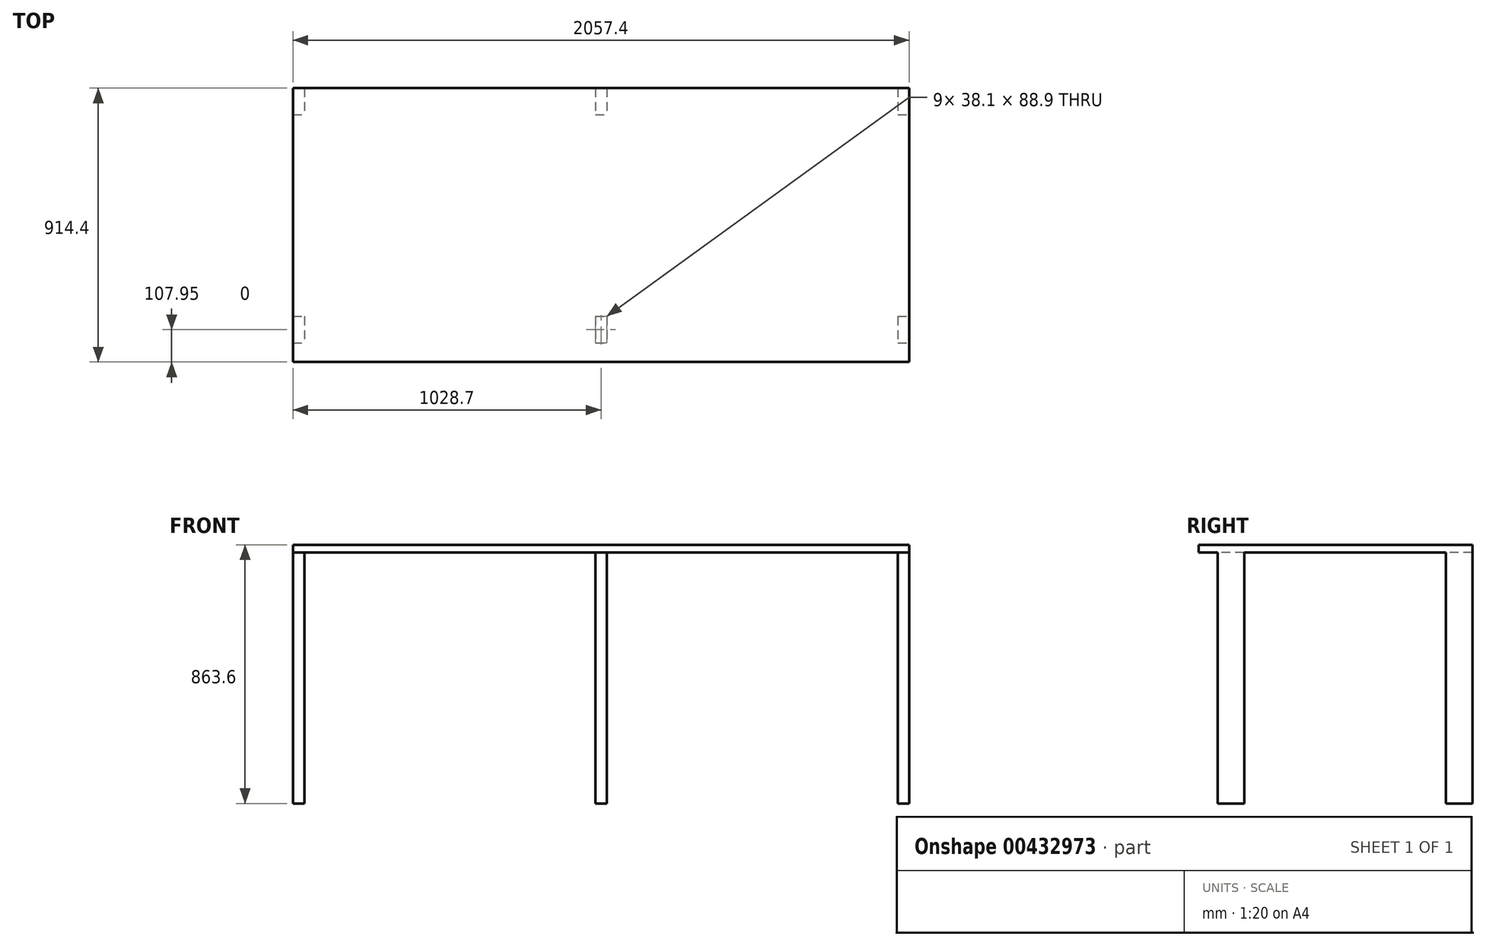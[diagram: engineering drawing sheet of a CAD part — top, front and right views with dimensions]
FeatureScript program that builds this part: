
annotation { "Feature Type Name" : "Feature", "Feature Type Description" : "" }
export const myFeature = defineFeature(function(context is Context, id is Id, definition is map)
    precondition{}
    {
        {
            var Q0;
            Q0=qCreatedBy(makeId("Top.planeOp"),FACE);
            var sketch = newSketch(context, id + "F0", { "sketchPlane" : qUnion([Q0])});
            skLineSegment(sketch, "E0.bottom", {"start": v(1028.7, 457.2) * mm, "end": v(-1028.7, 457.2) * mm});
            skLineSegment(sketch, "E0.top", {"start": v(1028.7, -457.2) * mm, "end": v(-1028.7, -457.2) * mm});
            skLineSegment(sketch, "E0.left", {"start": v(1028.7, 457.2) * mm, "end": v(1028.7, -457.2) * mm});
            skLineSegment(sketch, "E0.right", {"start": v(-1028.7, 457.2) * mm, "end": v(-1028.7, -457.2) * mm});
            skPoint(sketch, "E0.middle", {"position": v(0, 0) * mm});
            skSolve(sketch);
        }
        {
            var Q0;
            Q0=makeQuery(id+"F0.imprint","IMPRINT",FACE,{"disambiguationData":[TD([[makeQuery(id+"F0.imprint","IMPRINT",EDGE,{"derivedFrom":sQuery(id+"F0.wireOp",EDGE,"E0.bottom")}),1.0]])]});
            extrude(context, id + "F1", {"entities" : qUnion([Q0]), "oppositeDirection" : true, "depth" : 863.6 * mm});
        }
        {
            var Q0;
            Q0=makeQuery(id+"F1.opExtrude","SWEPT_FACE",FACE,{"disambiguationData":[OSD([sQuery(id+"F0.wireOp",EDGE,"E0.left")])]});
            var sketch = newSketch(context, id + "F2", { "sketchPlane" : qUnion([Q0])});
            skLineSegment(sketch, "E1", {"start": v(-457.2, 0) * mm, "end": v(-457.2, -25.4) * mm});
            skLineSegment(sketch, "E2", {"start": v(-457.2, -25.4) * mm, "end": v(-393.7, -25.4) * mm});
            skLineSegment(sketch, "E3", {"start": v(-393.7, -25.4) * mm, "end": v(-393.7, -863.6) * mm});
            skLineSegment(sketch, "E4", {"start": v(-393.7, -863.6) * mm, "end": v(-457.2, -863.6) * mm});
            skLineSegment(sketch, "E5", {"start": v(-457.2, -863.6) * mm, "end": v(-457.2, -25.4) * mm});
            skLineSegment(sketch, "E6", {"start": v(-393.7, -25.4) * mm, "end": v(457.2, -25.4) * mm});
            skLineSegment(sketch, "E7", {"start": v(-393.7, -25.4) * mm, "end": v(-304.8, -25.4) * mm});
            skLineSegment(sketch, "E8", {"start": v(-304.8, -25.4) * mm, "end": v(-304.8, -863.6) * mm});
            skLineSegment(sketch, "E9", {"start": v(-304.8, -863.6) * mm, "end": v(368.3, -863.6) * mm});
            skLineSegment(sketch, "E10", {"start": v(368.3, -863.6) * mm, "end": v(368.3, -25.4) * mm});
            skSolve(sketch);
        }
        {
            var Q0;
            Q0=makeQuery(id+"F2.imprint","IMPRINT",FACE,{"disambiguationData":[TD([[makeQuery(id+"F2.imprint","IMPRINT",EDGE,{"derivedFrom":sQuery(id+"F2.wireOp",EDGE,"E2")}),-1.0]])]});
            var Q1;
            {var subQ0=sQuery(id+"F2.wireOp",EDGE,"E8");Q1=makeQuery(id+"F2.imprint","IMPRINT",FACE,{"disambiguationData":[TD([[makeQuery(id+"F2.imprint","IMPRINT",EDGE,{"derivedFrom":subQ0}),1.0]])]});}
            extrude(context, id + "F3", {"entities" : qUnion([Q0, Q1]), "operationType" : NewBodyOperationType.REMOVE, "endBound" : BoundingType.THROUGH_ALL, "oppositeDirection" : true, "depth" : 25.4 * mm});
        }
        {
            var Q0;
            Q0=makeQuery(id+"F3.boolean.opBoolean","COPY",FACE,{"derivedFrom":makeQuery(id+"F3.opExtrude","SWEPT_FACE",FACE,{"disambiguationData":[OSD([sQuery(id+"F2.wireOp",EDGE,"E3")])]})});
            var sketch = newSketch(context, id + "F4", { "sketchPlane" : qUnion([Q0])});
            skLineSegment(sketch, "E11", {"start": v(-1028.7, -863.6) * mm, "end": v(-990.6, -863.6) * mm});
            skLineSegment(sketch, "E12", {"start": v(-990.6, -863.6) * mm, "end": v(-990.6, -25.4) * mm});
            skLineSegment(sketch, "E13", {"start": v(-990.6, -25.4) * mm, "end": v(-19.05, -25.4) * mm});
            skLineSegment(sketch, "E14", {"start": v(-19.05, -25.4) * mm, "end": v(-19.05, -863.6) * mm});
            skLineSegment(sketch, "E15", {"start": v(-19.05, -863.6) * mm, "end": v(-990.6, -863.6) * mm});
            skLineSegment(sketch, "E16.MirrorCS", {"start": v(19.05, -25.4) * mm, "end": v(19.05, -863.6) * mm});
            skLineSegment(sketch, "E17.MirrorCS", {"start": v(990.6, -25.4) * mm, "end": v(19.05, -25.4) * mm});
            skLineSegment(sketch, "E18.MirrorCS", {"start": v(990.6, -863.6) * mm, "end": v(990.6, -25.4) * mm});
            skLineSegment(sketch, "E19.MirrorCS", {"start": v(19.05, -863.6) * mm, "end": v(990.6, -863.6) * mm});
            skSolve(sketch);
        }
        {
            var Q0;
            Q0=makeQuery(id+"F4.imprint","IMPRINT",FACE,{"disambiguationData":[TD([[makeQuery(id+"F4.imprint","IMPRINT",EDGE,{"derivedFrom":sQuery(id+"F4.wireOp",EDGE,"E12")}),-1.0]])]});
            var Q1;
            Q1=makeQuery(id+"F4.imprint","IMPRINT",FACE,{"disambiguationData":[TD([[makeQuery(id+"F4.imprint","IMPRINT",EDGE,{"derivedFrom":sQuery(id+"F4.wireOp",EDGE,"E16.MirrorCS")}),1.0]])]});
            extrude(context, id + "F5", {"entities" : qUnion([Q0, Q1]), "operationType" : NewBodyOperationType.REMOVE, "endBound" : BoundingType.THROUGH_ALL, "oppositeDirection" : true, "depth" : 25.4 * mm});
        }
    });
